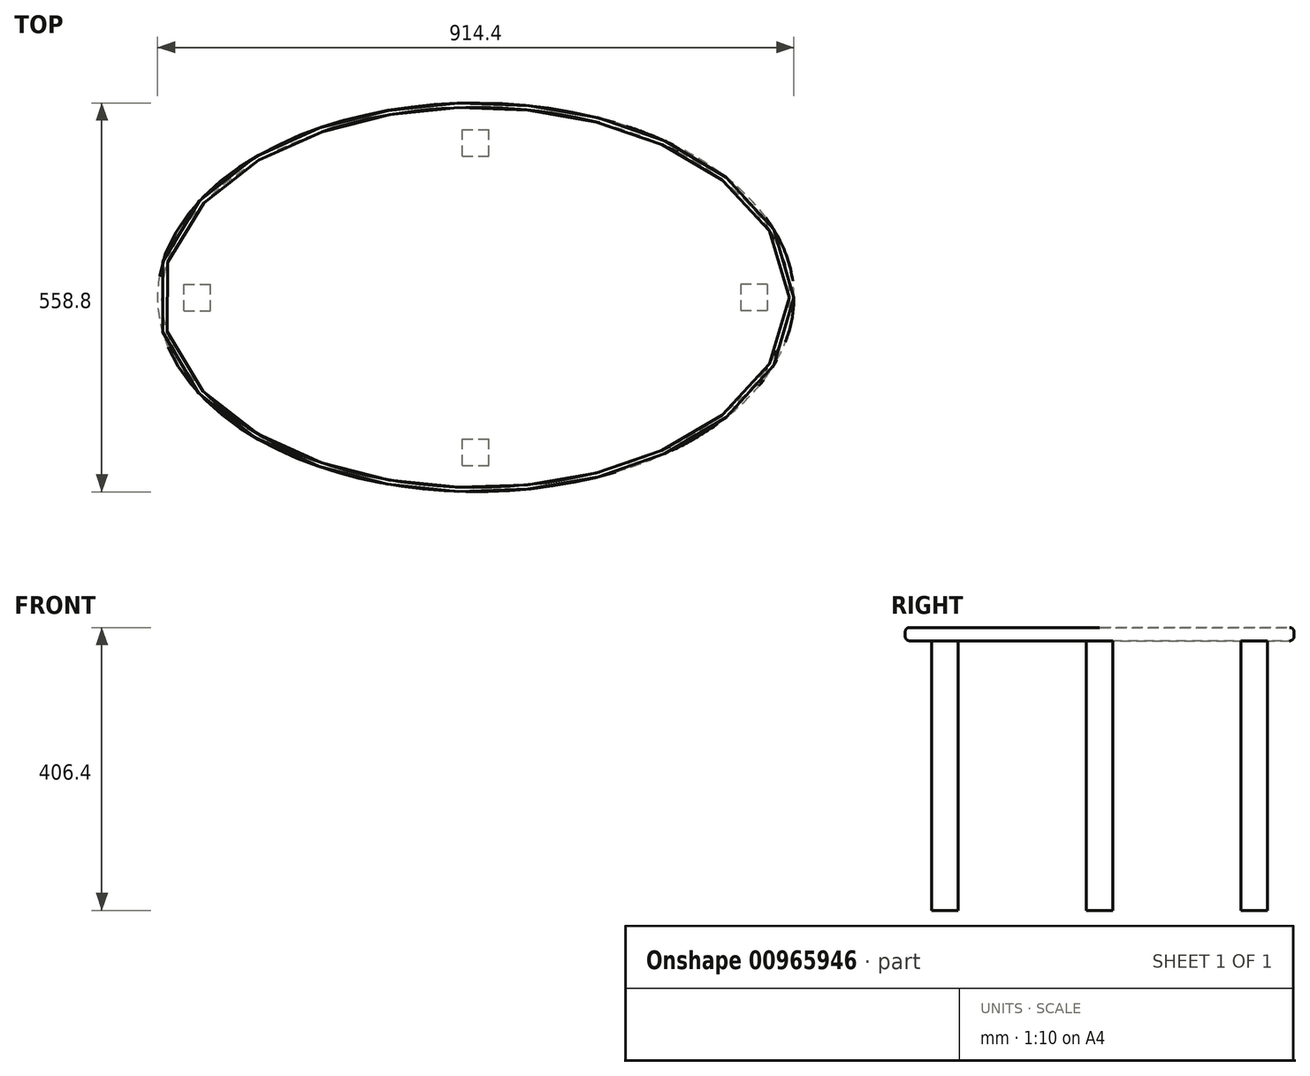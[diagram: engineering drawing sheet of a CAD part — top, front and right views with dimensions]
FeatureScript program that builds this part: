
annotation { "Feature Type Name" : "Feature", "Feature Type Description" : "" }
export const myFeature = defineFeature(function(context is Context, id is Id, definition is map)
    precondition{}
    {
        {
            var Q0;
            Q0=qCreatedBy(makeId("Top.planeOp"),FACE);
            var sketch = newSketch(context, id + "F0", { "sketchPlane" : qUnion([Q0])});
            skEllipse(sketch, "E0", {"center": v(0, 0) * mm, "majorRadius": 457.2 * mm, "minorRadius": 279.4 * mm, "majorAxis": v(1, 0)});
            skSolve(sketch);
        }
        {
            var Q0;
            Q0 = qSketchRegion(id + "F0", true);
            extrude(context, id + "F1", {"entities" : qUnion([Q0]), "depth" : 19.05 * mm, "offsetDistance" : 25.4 * mm});
        }
        {
            var Q0;
            Q0=makeQuery(id+"F1.opExtrude","CAP_EDGE",EDGE,{"disambiguationData":[OSD([sQuery(id+"F0.wireOp",EDGE,"E0")])],"isStart":false});
            var Q1;
            Q1=makeQuery(id+"F1.opExtrude","CAP_EDGE",EDGE,{"disambiguationData":[OSD([sQuery(id+"F0.wireOp",EDGE,"E0")])],"isStart":true});
            fillet(context, id + "F2", {"entities" : qUnion([Q0, Q1]), "radius" : 6.35 * mm, "tangentPropagation" : true, "allowEdgeOverflow" : false});
        }
        {
            var Q0;
            Q0=makeQuery(id+"F1.opExtrude","CAP_FACE",FACE,{"disambiguationData":[OSD([sQuery(id+"F0.wireOp",EDGE,"E0")])],"isStart":true});
            var sketch = newSketch(context, id + "F3", { "sketchPlane" : qUnion([Q0])});
            skLineSegment(sketch, "E1.bottom", {"start": v(419.1, -19.05) * mm, "end": v(381, -19.05) * mm});
            skLineSegment(sketch, "E1.top", {"start": v(419.1, 19.05) * mm, "end": v(381, 19.05) * mm});
            skLineSegment(sketch, "E1.left", {"start": v(419.1, -19.05) * mm, "end": v(419.1, 19.05) * mm});
            skLineSegment(sketch, "E1.right", {"start": v(381, -19.05) * mm, "end": v(381, 19.05) * mm});
            skSolve(sketch);
        }
        {
            var Q0;
            Q0 = qSketchRegion(id + "F3", true);
            extrude(context, id + "F4", {"entities" : qUnion([Q0]), "depth" : 387.35 * mm, "offsetDistance" : 25.4 * mm});
        }
        {
            var Q0;
            Q0=makeQuery(id+"F1.opExtrude","CAP_FACE",FACE,{"disambiguationData":[OSD([sQuery(id+"F0.wireOp",EDGE,"E0")])],"isStart":true});
            var sketch = newSketch(context, id + "F5", { "sketchPlane" : qUnion([Q0])});
            skLineSegment(sketch, "E2.bottom", {"start": v(-419.1, 19.05) * mm, "end": v(-381, 19.05) * mm});
            skLineSegment(sketch, "E2.top", {"start": v(-419.1, -19.05) * mm, "end": v(-381, -19.05) * mm});
            skLineSegment(sketch, "E2.left", {"start": v(-419.1, 19.05) * mm, "end": v(-419.1, -19.05) * mm});
            skLineSegment(sketch, "E2.right", {"start": v(-381, 19.05) * mm, "end": v(-381, -19.05) * mm});
            skSolve(sketch);
        }
        {
            var Q0;
            Q0 = qSketchRegion(id + "F5", true);
            extrude(context, id + "F6", {"entities" : qUnion([Q0]), "depth" : 387.35 * mm, "offsetDistance" : 25.4 * mm});
        }
        {
            var Q0;
            Q0=makeQuery(id+"F1.opExtrude","CAP_FACE",FACE,{"disambiguationData":[OSD([sQuery(id+"F0.wireOp",EDGE,"E0")])],"isStart":true});
            var sketch = newSketch(context, id + "F7", { "sketchPlane" : qUnion([Q0])});
            skLineSegment(sketch, "E3.bottom", {"start": v(-19.05, 241.3) * mm, "end": v(19.05, 241.3) * mm});
            skLineSegment(sketch, "E3.top", {"start": v(-19.05, 203.2) * mm, "end": v(19.05, 203.2) * mm});
            skLineSegment(sketch, "E3.left", {"start": v(-19.05, 241.3) * mm, "end": v(-19.05, 203.2) * mm});
            skLineSegment(sketch, "E3.right", {"start": v(19.05, 241.3) * mm, "end": v(19.05, 203.2) * mm});
            skSolve(sketch);
        }
        {
            var Q0;
            Q0 = qSketchRegion(id + "F7", true);
            extrude(context, id + "F8", {"entities" : qUnion([Q0]), "depth" : 387.35 * mm, "offsetDistance" : 25.4 * mm});
        }
        {
            var Q0;
            Q0=makeQuery(id+"F1.opExtrude","CAP_FACE",FACE,{"disambiguationData":[OSD([sQuery(id+"F0.wireOp",EDGE,"E0")])],"isStart":true});
            var sketch = newSketch(context, id + "F9", { "sketchPlane" : qUnion([Q0])});
            skLineSegment(sketch, "E4.bottom", {"start": v(-19.05, -203.2) * mm, "end": v(19.05, -203.2) * mm});
            skLineSegment(sketch, "E4.top", {"start": v(-19.05, -241.3) * mm, "end": v(19.05, -241.3) * mm});
            skLineSegment(sketch, "E4.left", {"start": v(-19.05, -203.2) * mm, "end": v(-19.05, -241.3) * mm});
            skLineSegment(sketch, "E4.right", {"start": v(19.05, -203.2) * mm, "end": v(19.05, -241.3) * mm});
            skSolve(sketch);
        }
        {
            var Q0;
            Q0 = qSketchRegion(id + "F9", true);
            extrude(context, id + "F10", {"entities" : qUnion([Q0]), "depth" : 387.35 * mm, "offsetDistance" : 25.4 * mm});
        }
    });
